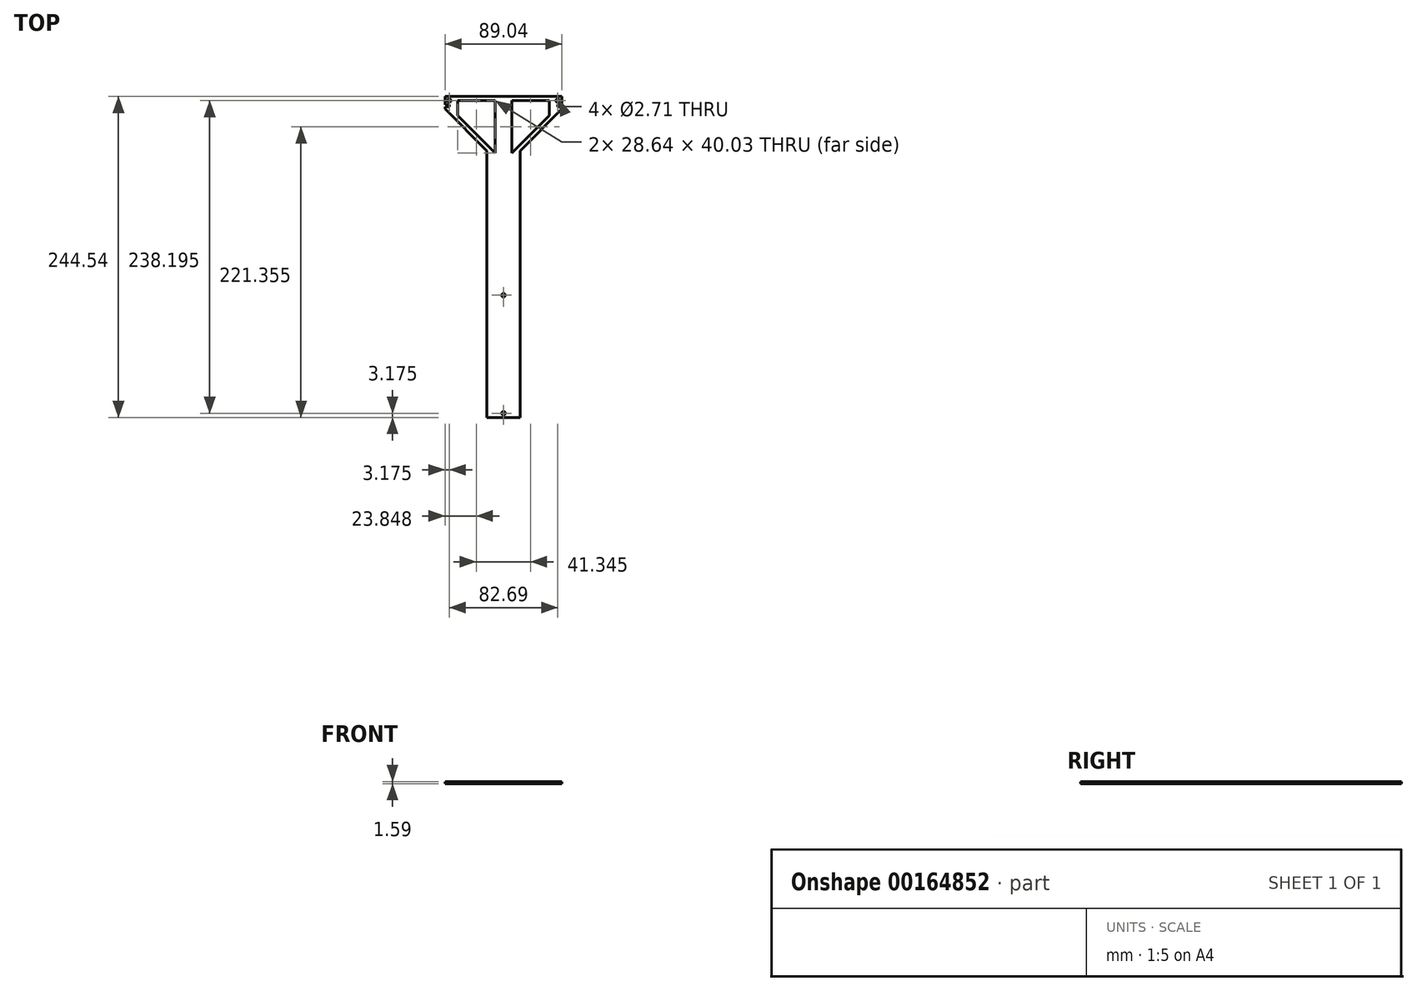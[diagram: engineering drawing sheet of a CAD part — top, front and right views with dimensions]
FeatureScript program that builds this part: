
annotation { "Feature Type Name" : "Feature", "Feature Type Description" : "" }
export const myFeature = defineFeature(function(context is Context, id is Id, definition is map)
    precondition{}
    {
        {
            var Q0;
            Q0=qCreatedBy(makeId("Top.planeOp"),FACE);
            var sketch = newSketch(context, id + "F0", { "sketchPlane" : qUnion([Q0])});
            skLineSegment(sketch, "E0.bottom", {"start": v(0, 0) * mm, "end": v(25.4, 0) * mm, "construction": true});
            skLineSegment(sketch, "E0.top", {"start": v(0, -203.2) * mm, "end": v(25.4, -203.2) * mm});
            skLineSegment(sketch, "E0.left", {"start": v(0, 0) * mm, "end": v(0, -203.2) * mm});
            skLineSegment(sketch, "E0.right", {"start": v(25.4, 0) * mm, "end": v(25.4, -203.2) * mm});
            skLineSegment(sketch, "E1", {"start": v(12.7, -110.14) * mm, "end": v(12.7, -200.03) * mm, "construction": true});
            skCircle(sketch, "E2", {"center": v(12.7, -110.14) * mm, "radius": 1.35 * mm});
            skCircle(sketch, "E3", {"center": v(12.7, -200.03) * mm, "radius": 1.35 * mm});
            skLineSegment(sketch, "E4", {"start": v(12.7, -200.03) * mm, "end": v(12.7, -203.2) * mm, "construction": true});
            skLineSegment(sketch, "E5", {"start": v(12.7, 0) * mm, "end": v(12.7, 38.17) * mm, "construction": true});
            skLineSegment(sketch, "E6", {"start": v(-28.64, 38.17) * mm, "end": v(54.04, 38.17) * mm, "construction": true});
            skCircle(sketch, "E7", {"center": v(-28.64, 38.17) * mm, "radius": 1.35 * mm});
            skCircle(sketch, "E8", {"center": v(54.04, 38.17) * mm, "radius": 1.35 * mm});
            skLineSegment(sketch, "E9", {"start": v(0, 0) * mm, "end": v(-31.82, 31.82) * mm});
            skLineSegment(sketch, "E10", {"start": v(-31.82, 31.82) * mm, "end": v(-31.82, 41.34) * mm});
            skLineSegment(sketch, "E11", {"start": v(-31.82, 41.34) * mm, "end": v(57.22, 41.34) * mm});
            skLineSegment(sketch, "E12", {"start": v(57.22, 41.34) * mm, "end": v(57.22, 31.82) * mm});
            skLineSegment(sketch, "E13", {"start": v(57.22, 31.82) * mm, "end": v(25.4, 0) * mm});
            skLineSegment(sketch, "E14", {"start": v(-28.64, 38.17) * mm, "end": v(-28.64, 31.82) * mm, "construction": true});
            skLineSegment(sketch, "E15", {"start": v(-28.64, 31.82) * mm, "end": v(-31.82, 31.82) * mm, "construction": true});
            skLineSegment(sketch, "E16", {"start": v(12.7, 38.17) * mm, "end": v(12.7, 41.34) * mm, "construction": true});
            skSolve(sketch);
        }
        {
            var Q0;
            Q0 = qSketchRegion(id + "F0", true);
            extrude(context, id + "F1", {"entities" : qUnion([Q0]), "depth" : 1.59 * mm});
        }
        {
            var Q0;
            Q0=makeQuery(id+"F1.opExtrude","CAP_FACE",FACE,{"disambiguationData":[OSD([sQuery(id+"F0.wireOp",EDGE,"E0.top"),sQuery(id+"F0.wireOp",EDGE,"E0.left"),sQuery(id+"F0.wireOp",EDGE,"E0.right"),sQuery(id+"F0.wireOp",EDGE,"E2"),sQuery(id+"F0.wireOp",EDGE,"E3"),sQuery(id+"F0.wireOp",EDGE,"E7"),sQuery(id+"F0.wireOp",EDGE,"E8"),sQuery(id+"F0.wireOp",EDGE,"E9"),sQuery(id+"F0.wireOp",EDGE,"E10"),sQuery(id+"F0.wireOp",EDGE,"E11"),sQuery(id+"F0.wireOp",EDGE,"E12"),sQuery(id+"F0.wireOp",EDGE,"E13")])],"isStart":false});
            var sketch = newSketch(context, id + "F2", { "sketchPlane" : qUnion([Q0])});
            skLineSegment(sketch, "E17.bottom", {"start": v(-31.82, 35) * mm, "end": v(-28.64, 35) * mm});
            skLineSegment(sketch, "E17.top", {"start": v(-31.82, 33.4) * mm, "end": v(-28.64, 33.4) * mm});
            skLineSegment(sketch, "E17.left", {"start": v(-31.82, 35) * mm, "end": v(-31.82, 33.4) * mm});
            skLineSegment(sketch, "E17.right", {"start": v(-28.64, 35) * mm, "end": v(-28.64, 33.4) * mm});
            skLineSegment(sketch, "E18.bottom", {"start": v(57.22, 35) * mm, "end": v(54.04, 35) * mm});
            skLineSegment(sketch, "E18.top", {"start": v(57.22, 33.4) * mm, "end": v(54.04, 33.4) * mm});
            skLineSegment(sketch, "E18.left", {"start": v(57.22, 35) * mm, "end": v(57.22, 33.4) * mm});
            skLineSegment(sketch, "E18.right", {"start": v(54.04, 35) * mm, "end": v(54.04, 33.4) * mm});
            skLineSegment(sketch, "E19", {"start": v(-28.64, 35) * mm, "end": v(-28.64, 38.17) * mm, "construction": true});
            skLineSegment(sketch, "E20", {"start": v(12.7, 41.34) * mm, "end": v(12.7, 38.17) * mm, "construction": true});
            skLineSegment(sketch, "E21", {"start": v(-15.9, 15.9) * mm, "end": v(-13.66, 18.15) * mm, "construction": true});
            skLineSegment(sketch, "E22", {"start": v(41.3, 15.9) * mm, "end": v(39.06, 18.15) * mm, "construction": true});
            skLineSegment(sketch, "E23", {"start": v(6.35, 38.17) * mm, "end": v(19.05, 38.17) * mm, "construction": true});
            skLineSegment(sketch, "E24", {"start": v(-22.3, 26.78) * mm, "end": v(6.35, -1.86) * mm});
            skLineSegment(sketch, "E25", {"start": v(6.35, -1.86) * mm, "end": v(6.35, 38.17) * mm});
            skLineSegment(sketch, "E26", {"start": v(6.35, 38.17) * mm, "end": v(-22.3, 38.17) * mm});
            skLineSegment(sketch, "E27", {"start": v(-22.3, 38.17) * mm, "end": v(-22.3, 26.78) * mm});
            skLineSegment(sketch, "E28", {"start": v(-28.64, 38.17) * mm, "end": v(-22.3, 38.17) * mm, "construction": true});
            skLineSegment(sketch, "E29", {"start": v(19.05, 38.17) * mm, "end": v(19.05, -1.86) * mm});
            skLineSegment(sketch, "E30", {"start": v(19.05, -1.86) * mm, "end": v(47.7, 26.78) * mm});
            skLineSegment(sketch, "E31", {"start": v(47.7, 26.78) * mm, "end": v(47.7, 38.17) * mm});
            skLineSegment(sketch, "E32", {"start": v(47.7, 38.17) * mm, "end": v(19.05, 38.17) * mm});
            skSolve(sketch);
        }
        {
            var Q0;
            Q0 = qSketchRegion(id + "F2", true);
            var Q1;
            Q1=makeQuery(id+"F1.opExtrude","CAP_FACE",FACE,{"disambiguationData":[OSD([sQuery(id+"F0.wireOp",EDGE,"E0.top"),sQuery(id+"F0.wireOp",EDGE,"E0.left"),sQuery(id+"F0.wireOp",EDGE,"E0.right"),sQuery(id+"F0.wireOp",EDGE,"E2"),sQuery(id+"F0.wireOp",EDGE,"E3"),sQuery(id+"F0.wireOp",EDGE,"E7"),sQuery(id+"F0.wireOp",EDGE,"E8"),sQuery(id+"F0.wireOp",EDGE,"E9"),sQuery(id+"F0.wireOp",EDGE,"E10"),sQuery(id+"F0.wireOp",EDGE,"E11"),sQuery(id+"F0.wireOp",EDGE,"E12"),sQuery(id+"F0.wireOp",EDGE,"E13")])],"isStart":true});
            extrude(context, id + "F3", {"entities" : qUnion([Q0]), "operationType" : NewBodyOperationType.REMOVE, "endBound" : BoundingType.UP_TO_SURFACE, "oppositeDirection" : true, "endBoundEntityFace" : qUnion([Q1]), "depth" : 25.4 * mm});
        }
    });
